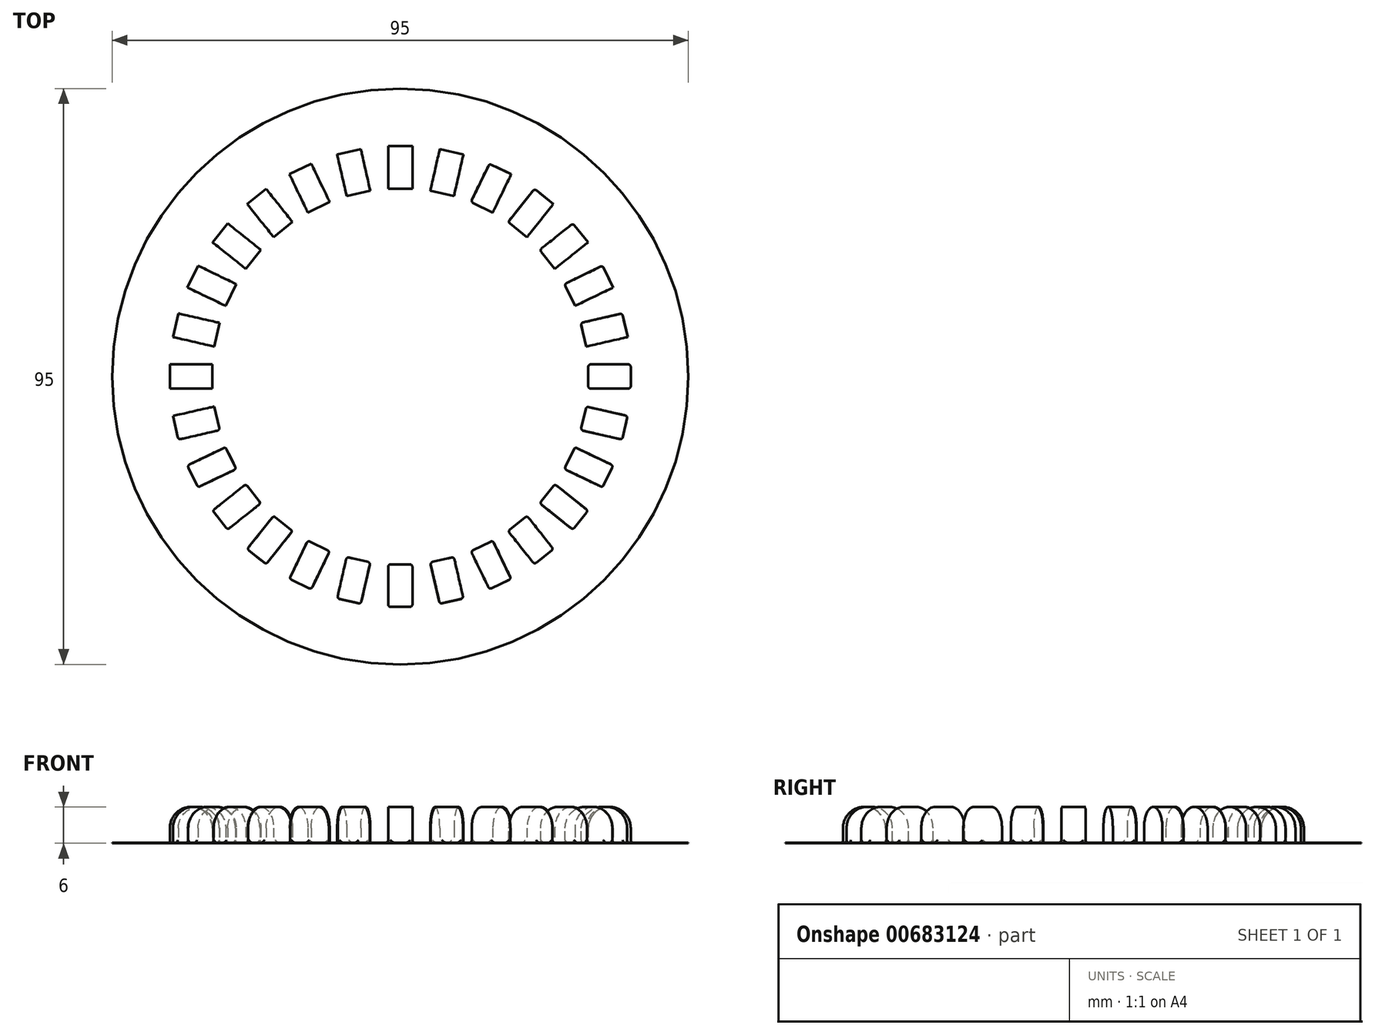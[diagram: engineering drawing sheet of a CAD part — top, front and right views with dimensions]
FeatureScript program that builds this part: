
annotation { "Feature Type Name" : "Feature", "Feature Type Description" : "" }
export const myFeature = defineFeature(function(context is Context, id is Id, definition is map)
    precondition{}
    {
        {
            var Q0;
            Q0=qCreatedBy(makeId("Top.planeOp"),FACE);
            var sketch = newSketch(context, id + "F0", { "sketchPlane" : qUnion([Q0])});
            skCircle(sketch, "E0", {"center": v(0, 0) * mm, "radius": 47.5 * mm});
            skSolve(sketch);
        }
        {
            var Q0;
            Q0=makeQuery(id+"F0.imprint","IMPRINT",FACE,{"disambiguationData":[TD([[makeQuery(id+"F0.imprint","IMPRINT",EDGE,{"derivedFrom":sQuery(id+"F0.wireOp",EDGE,"E0")}),1.0]])]});
            extrude(context, id + "F1", {"entities" : qUnion([Q0]), "depth" : .1 * mm, "offsetDistance" : 25 * mm});
        }
        {
            var Q0;
            Q0=qCreatedBy(makeId("Top.planeOp"),FACE);
            var sketch = newSketch(context, id + "F2", { "sketchPlane" : qUnion([Q0])});
            skLineSegment(sketch, "E1", {"start": v(0, 0) * mm, "end": v(0, 49.65) * mm, "construction": true});
            skLineSegment(sketch, "E2.bottom", {"start": v(-2, 38) * mm, "end": v(2, 38) * mm});
            skLineSegment(sketch, "E2.top", {"start": v(-2, 31) * mm, "end": v(2, 31) * mm});
            skLineSegment(sketch, "E2.left", {"start": v(-2, 38) * mm, "end": v(-2, 31) * mm});
            skLineSegment(sketch, "E2.right", {"start": v(2, 38) * mm, "end": v(2, 31) * mm});
            skPoint(sketch, "E3", {"position": v(0, 38) * mm});
            skPoint(sketch, "E4.1.0", {"position": v(-8.46, 37.05) * mm});
            skLineSegment(sketch, "E4.1.1", {"start": v(-8.85, 29.78) * mm, "end": v(-4.95, 30.67) * mm});
            skLineSegment(sketch, "E4.1.2", {"start": v(-10.4, 36.6) * mm, "end": v(-8.85, 29.78) * mm});
            skLineSegment(sketch, "E4.1.3", {"start": v(-6.5, 37.5) * mm, "end": v(-4.95, 30.67) * mm});
            skLineSegment(sketch, "E4.1.4", {"start": v(-10.4, 36.6) * mm, "end": v(-6.5, 37.5) * mm});
            skPoint(sketch, "E4.2.0", {"position": v(-16.49, 34.24) * mm});
            skLineSegment(sketch, "E4.2.1", {"start": v(-15.25, 27.06) * mm, "end": v(-11.65, 28.8) * mm});
            skLineSegment(sketch, "E4.2.2", {"start": v(-18.29, 33.37) * mm, "end": v(-15.25, 27.06) * mm});
            skLineSegment(sketch, "E4.2.3", {"start": v(-14.69, 35.1) * mm, "end": v(-11.65, 28.8) * mm});
            skLineSegment(sketch, "E4.2.4", {"start": v(-18.29, 33.37) * mm, "end": v(-14.69, 35.1) * mm});
            skPoint(sketch, "E4.center", {"position": v(0, 0) * mm});
            skLineSegment(sketch, "E5.1.3.0", {"start": v(-20.9, 22.99) * mm, "end": v(-17.76, 25.48) * mm});
            skPoint(sketch, "E5.2.3.0", {"position": v(-23.7, 29.7) * mm});
            skLineSegment(sketch, "E5.4.3.0", {"start": v(-25.26, 28.46) * mm, "end": v(-20.9, 22.99) * mm});
            skLineSegment(sketch, "E5.7.3.0", {"start": v(-22.13, 30.96) * mm, "end": v(-17.76, 25.48) * mm});
            skLineSegment(sketch, "E5.10.3.0", {"start": v(-25.26, 28.46) * mm, "end": v(-22.13, 30.96) * mm});
            skLineSegment(sketch, "E5.1.4.0", {"start": v(-25.48, 17.76) * mm, "end": v(-22.99, 20.9) * mm});
            skPoint(sketch, "E5.2.4.0", {"position": v(-29.7, 23.7) * mm});
            skLineSegment(sketch, "E5.4.4.0", {"start": v(-30.96, 22.13) * mm, "end": v(-25.48, 17.76) * mm});
            skLineSegment(sketch, "E5.7.4.0", {"start": v(-28.46, 25.26) * mm, "end": v(-22.99, 20.9) * mm});
            skLineSegment(sketch, "E5.10.4.0", {"start": v(-30.96, 22.13) * mm, "end": v(-28.46, 25.26) * mm});
            skLineSegment(sketch, "E5.1.5.0", {"start": v(-28.8, 11.65) * mm, "end": v(-27.06, 15.25) * mm});
            skPoint(sketch, "E5.2.5.0", {"position": v(-34.24, 16.49) * mm});
            skLineSegment(sketch, "E5.4.5.0", {"start": v(-35.1, 14.69) * mm, "end": v(-28.8, 11.65) * mm});
            skLineSegment(sketch, "E5.7.5.0", {"start": v(-33.37, 18.29) * mm, "end": v(-27.06, 15.25) * mm});
            skLineSegment(sketch, "E5.10.5.0", {"start": v(-35.1, 14.69) * mm, "end": v(-33.37, 18.29) * mm});
            skLineSegment(sketch, "E5.1.6.0", {"start": v(-30.67, 4.95) * mm, "end": v(-29.78, 8.85) * mm});
            skPoint(sketch, "E5.2.6.0", {"position": v(-37.05, 8.46) * mm});
            skLineSegment(sketch, "E5.4.6.0", {"start": v(-37.5, 6.5) * mm, "end": v(-30.67, 4.95) * mm});
            skLineSegment(sketch, "E5.7.6.0", {"start": v(-36.6, 10.4) * mm, "end": v(-29.78, 8.85) * mm});
            skLineSegment(sketch, "E5.10.6.0", {"start": v(-37.5, 6.5) * mm, "end": v(-36.6, 10.4) * mm});
            skLineSegment(sketch, "E5.1.7.0", {"start": v(-31, -2) * mm, "end": v(-31, 2) * mm});
            skPoint(sketch, "E5.2.7.0", {"position": v(-38, 0) * mm});
            skLineSegment(sketch, "E5.4.7.0", {"start": v(-38, -2) * mm, "end": v(-31, -2) * mm});
            skLineSegment(sketch, "E5.7.7.0", {"start": v(-38, 2) * mm, "end": v(-31, 2) * mm});
            skLineSegment(sketch, "E5.10.7.0", {"start": v(-38, -2) * mm, "end": v(-38, 2) * mm});
            skLineSegment(sketch, "E5.1.8.0", {"start": v(-29.78, -8.85) * mm, "end": v(-30.67, -4.95) * mm});
            skPoint(sketch, "E5.2.8.0", {"position": v(-37.05, -8.46) * mm});
            skLineSegment(sketch, "E5.4.8.0", {"start": v(-36.6, -10.4) * mm, "end": v(-29.78, -8.85) * mm});
            skLineSegment(sketch, "E5.7.8.0", {"start": v(-37.5, -6.5) * mm, "end": v(-30.67, -4.95) * mm});
            skLineSegment(sketch, "E5.10.8.0", {"start": v(-36.6, -10.4) * mm, "end": v(-37.5, -6.5) * mm});
            skLineSegment(sketch, "E5.1.9.0", {"start": v(-27.06, -15.25) * mm, "end": v(-28.8, -11.65) * mm});
            skPoint(sketch, "E5.2.9.0", {"position": v(-34.24, -16.49) * mm});
            skLineSegment(sketch, "E5.4.9.0", {"start": v(-33.37, -18.29) * mm, "end": v(-27.06, -15.25) * mm});
            skLineSegment(sketch, "E5.7.9.0", {"start": v(-35.1, -14.69) * mm, "end": v(-28.8, -11.65) * mm});
            skLineSegment(sketch, "E5.10.9.0", {"start": v(-33.37, -18.29) * mm, "end": v(-35.1, -14.69) * mm});
            skLineSegment(sketch, "E5.1.10.0", {"start": v(-22.99, -20.9) * mm, "end": v(-25.48, -17.76) * mm});
            skPoint(sketch, "E5.2.10.0", {"position": v(-29.7, -23.7) * mm});
            skLineSegment(sketch, "E5.4.10.0", {"start": v(-28.46, -25.26) * mm, "end": v(-22.99, -20.9) * mm});
            skLineSegment(sketch, "E5.7.10.0", {"start": v(-30.96, -22.13) * mm, "end": v(-25.48, -17.76) * mm});
            skLineSegment(sketch, "E5.10.10.0", {"start": v(-28.46, -25.26) * mm, "end": v(-30.96, -22.13) * mm});
            skLineSegment(sketch, "E5.1.11.0", {"start": v(-17.76, -25.48) * mm, "end": v(-20.9, -22.99) * mm});
            skPoint(sketch, "E5.2.11.0", {"position": v(-23.7, -29.7) * mm});
            skLineSegment(sketch, "E5.4.11.0", {"start": v(-22.13, -30.96) * mm, "end": v(-17.76, -25.48) * mm});
            skLineSegment(sketch, "E5.7.11.0", {"start": v(-25.26, -28.46) * mm, "end": v(-20.9, -22.99) * mm});
            skLineSegment(sketch, "E5.10.11.0", {"start": v(-22.13, -30.96) * mm, "end": v(-25.26, -28.46) * mm});
            skLineSegment(sketch, "E5.1.12.0", {"start": v(-11.65, -28.8) * mm, "end": v(-15.25, -27.06) * mm});
            skPoint(sketch, "E5.2.12.0", {"position": v(-16.49, -34.24) * mm});
            skLineSegment(sketch, "E5.4.12.0", {"start": v(-14.69, -35.1) * mm, "end": v(-11.65, -28.8) * mm});
            skLineSegment(sketch, "E5.7.12.0", {"start": v(-18.29, -33.37) * mm, "end": v(-15.25, -27.06) * mm});
            skLineSegment(sketch, "E5.10.12.0", {"start": v(-14.69, -35.1) * mm, "end": v(-18.29, -33.37) * mm});
            skLineSegment(sketch, "E5.1.13.0", {"start": v(-4.95, -30.67) * mm, "end": v(-8.85, -29.78) * mm});
            skPoint(sketch, "E5.2.13.0", {"position": v(-8.46, -37.05) * mm});
            skLineSegment(sketch, "E5.4.13.0", {"start": v(-6.5, -37.5) * mm, "end": v(-4.95, -30.67) * mm});
            skLineSegment(sketch, "E5.7.13.0", {"start": v(-10.4, -36.6) * mm, "end": v(-8.85, -29.78) * mm});
            skLineSegment(sketch, "E5.10.13.0", {"start": v(-6.5, -37.5) * mm, "end": v(-10.4, -36.6) * mm});
            skLineSegment(sketch, "E5.1.14.0", {"start": v(2, -31) * mm, "end": v(-2, -31) * mm});
            skPoint(sketch, "E5.2.14.0", {"position": v(0, -38) * mm});
            skLineSegment(sketch, "E5.4.14.0", {"start": v(2, -38) * mm, "end": v(2, -31) * mm});
            skLineSegment(sketch, "E5.7.14.0", {"start": v(-2, -38) * mm, "end": v(-2, -31) * mm});
            skLineSegment(sketch, "E5.10.14.0", {"start": v(2, -38) * mm, "end": v(-2, -38) * mm});
            skLineSegment(sketch, "E5.1.15.0", {"start": v(8.85, -29.78) * mm, "end": v(4.95, -30.67) * mm});
            skPoint(sketch, "E5.2.15.0", {"position": v(8.46, -37.05) * mm});
            skLineSegment(sketch, "E5.4.15.0", {"start": v(10.4, -36.6) * mm, "end": v(8.85, -29.78) * mm});
            skLineSegment(sketch, "E5.7.15.0", {"start": v(6.5, -37.5) * mm, "end": v(4.95, -30.67) * mm});
            skLineSegment(sketch, "E5.10.15.0", {"start": v(10.4, -36.6) * mm, "end": v(6.5, -37.5) * mm});
            skLineSegment(sketch, "E5.1.16.0", {"start": v(15.25, -27.06) * mm, "end": v(11.65, -28.8) * mm});
            skPoint(sketch, "E5.2.16.0", {"position": v(16.49, -34.24) * mm});
            skLineSegment(sketch, "E5.4.16.0", {"start": v(18.29, -33.37) * mm, "end": v(15.25, -27.06) * mm});
            skLineSegment(sketch, "E5.7.16.0", {"start": v(14.69, -35.1) * mm, "end": v(11.65, -28.8) * mm});
            skLineSegment(sketch, "E5.10.16.0", {"start": v(18.29, -33.37) * mm, "end": v(14.69, -35.1) * mm});
            skLineSegment(sketch, "E5.1.17.0", {"start": v(20.9, -22.99) * mm, "end": v(17.76, -25.48) * mm});
            skPoint(sketch, "E5.2.17.0", {"position": v(23.7, -29.7) * mm});
            skLineSegment(sketch, "E5.4.17.0", {"start": v(25.26, -28.46) * mm, "end": v(20.9, -22.99) * mm});
            skLineSegment(sketch, "E5.7.17.0", {"start": v(22.13, -30.96) * mm, "end": v(17.76, -25.48) * mm});
            skLineSegment(sketch, "E5.10.17.0", {"start": v(25.26, -28.46) * mm, "end": v(22.13, -30.96) * mm});
            skLineSegment(sketch, "E5.1.18.0", {"start": v(25.48, -17.76) * mm, "end": v(22.99, -20.9) * mm});
            skPoint(sketch, "E5.2.18.0", {"position": v(29.7, -23.7) * mm});
            skLineSegment(sketch, "E5.4.18.0", {"start": v(30.96, -22.13) * mm, "end": v(25.48, -17.76) * mm});
            skLineSegment(sketch, "E5.7.18.0", {"start": v(28.46, -25.26) * mm, "end": v(22.99, -20.9) * mm});
            skLineSegment(sketch, "E5.10.18.0", {"start": v(30.96, -22.13) * mm, "end": v(28.46, -25.26) * mm});
            skLineSegment(sketch, "E5.1.19.0", {"start": v(28.8, -11.65) * mm, "end": v(27.06, -15.25) * mm});
            skPoint(sketch, "E5.2.19.0", {"position": v(34.24, -16.49) * mm});
            skLineSegment(sketch, "E5.4.19.0", {"start": v(35.1, -14.69) * mm, "end": v(28.8, -11.65) * mm});
            skLineSegment(sketch, "E5.7.19.0", {"start": v(33.37, -18.29) * mm, "end": v(27.06, -15.25) * mm});
            skLineSegment(sketch, "E5.10.19.0", {"start": v(35.1, -14.69) * mm, "end": v(33.37, -18.29) * mm});
            skLineSegment(sketch, "E5.1.20.0", {"start": v(30.67, -4.95) * mm, "end": v(29.78, -8.85) * mm});
            skPoint(sketch, "E5.2.20.0", {"position": v(37.05, -8.46) * mm});
            skLineSegment(sketch, "E5.4.20.0", {"start": v(37.5, -6.5) * mm, "end": v(30.67, -4.95) * mm});
            skLineSegment(sketch, "E5.7.20.0", {"start": v(36.6, -10.4) * mm, "end": v(29.78, -8.85) * mm});
            skLineSegment(sketch, "E5.10.20.0", {"start": v(37.5, -6.5) * mm, "end": v(36.6, -10.4) * mm});
            skLineSegment(sketch, "E5.1.21.0", {"start": v(31, 2) * mm, "end": v(31, -2) * mm});
            skPoint(sketch, "E5.2.21.0", {"position": v(38, 0) * mm});
            skLineSegment(sketch, "E5.4.21.0", {"start": v(38, 2) * mm, "end": v(31, 2) * mm});
            skLineSegment(sketch, "E5.7.21.0", {"start": v(38, -2) * mm, "end": v(31, -2) * mm});
            skLineSegment(sketch, "E5.10.21.0", {"start": v(38, 2) * mm, "end": v(38, -2) * mm});
            skLineSegment(sketch, "E5.1.22.0", {"start": v(29.78, 8.85) * mm, "end": v(30.67, 4.95) * mm});
            skPoint(sketch, "E5.2.22.0", {"position": v(37.05, 8.46) * mm});
            skLineSegment(sketch, "E5.4.22.0", {"start": v(36.6, 10.4) * mm, "end": v(29.78, 8.85) * mm});
            skLineSegment(sketch, "E5.7.22.0", {"start": v(37.5, 6.5) * mm, "end": v(30.67, 4.95) * mm});
            skLineSegment(sketch, "E5.10.22.0", {"start": v(36.6, 10.4) * mm, "end": v(37.5, 6.5) * mm});
            skLineSegment(sketch, "E5.1.23.0", {"start": v(27.06, 15.25) * mm, "end": v(28.8, 11.65) * mm});
            skPoint(sketch, "E5.2.23.0", {"position": v(34.24, 16.49) * mm});
            skLineSegment(sketch, "E5.4.23.0", {"start": v(33.37, 18.29) * mm, "end": v(27.06, 15.25) * mm});
            skLineSegment(sketch, "E5.7.23.0", {"start": v(35.1, 14.69) * mm, "end": v(28.8, 11.65) * mm});
            skLineSegment(sketch, "E5.10.23.0", {"start": v(33.37, 18.29) * mm, "end": v(35.1, 14.69) * mm});
            skLineSegment(sketch, "E5.1.24.0", {"start": v(22.99, 20.9) * mm, "end": v(25.48, 17.76) * mm});
            skPoint(sketch, "E5.2.24.0", {"position": v(29.7, 23.7) * mm});
            skLineSegment(sketch, "E5.4.24.0", {"start": v(28.46, 25.26) * mm, "end": v(22.99, 20.9) * mm});
            skLineSegment(sketch, "E5.7.24.0", {"start": v(30.96, 22.13) * mm, "end": v(25.48, 17.76) * mm});
            skLineSegment(sketch, "E5.10.24.0", {"start": v(28.46, 25.26) * mm, "end": v(30.96, 22.13) * mm});
            skLineSegment(sketch, "E5.1.25.0", {"start": v(17.76, 25.48) * mm, "end": v(20.9, 22.99) * mm});
            skPoint(sketch, "E5.2.25.0", {"position": v(23.7, 29.7) * mm});
            skLineSegment(sketch, "E5.4.25.0", {"start": v(22.13, 30.96) * mm, "end": v(17.76, 25.48) * mm});
            skLineSegment(sketch, "E5.7.25.0", {"start": v(25.26, 28.46) * mm, "end": v(20.9, 22.99) * mm});
            skLineSegment(sketch, "E5.10.25.0", {"start": v(22.13, 30.96) * mm, "end": v(25.26, 28.46) * mm});
            skLineSegment(sketch, "E5.1.26.0", {"start": v(11.65, 28.8) * mm, "end": v(15.25, 27.06) * mm});
            skPoint(sketch, "E5.2.26.0", {"position": v(16.49, 34.24) * mm});
            skLineSegment(sketch, "E5.4.26.0", {"start": v(14.69, 35.1) * mm, "end": v(11.65, 28.8) * mm});
            skLineSegment(sketch, "E5.7.26.0", {"start": v(18.29, 33.37) * mm, "end": v(15.25, 27.06) * mm});
            skLineSegment(sketch, "E5.10.26.0", {"start": v(14.69, 35.1) * mm, "end": v(18.29, 33.37) * mm});
            skLineSegment(sketch, "E5.1.27.0", {"start": v(4.95, 30.67) * mm, "end": v(8.85, 29.78) * mm});
            skPoint(sketch, "E5.2.27.0", {"position": v(8.46, 37.05) * mm});
            skLineSegment(sketch, "E5.4.27.0", {"start": v(6.5, 37.5) * mm, "end": v(4.95, 30.67) * mm});
            skLineSegment(sketch, "E5.7.27.0", {"start": v(10.4, 36.6) * mm, "end": v(8.85, 29.78) * mm});
            skLineSegment(sketch, "E5.10.27.0", {"start": v(6.5, 37.5) * mm, "end": v(10.4, 36.6) * mm});
            skSolve(sketch);
        }
        {
            var Q0;
            Q0=qSketchRegion(id+"F2",true);
            extrude(context, id + "F3", {"entities" : qUnion([Q0]), "operationType" : NewBodyOperationType.ADD, "depth" : 6 * mm, "offsetDistance" : 25 * mm});
        }
        {
            var Q0;
            Q0=makeQuery(id+"F3.opExtrude","CAP_EDGE",EDGE,{"disambiguationData":[OSD([sQuery(id+"F2.wireOp",EDGE,"E4.1.1")])],"isStart":false});
            var Q1;
            Q1=makeQuery(id+"F3.opExtrude","CAP_EDGE",EDGE,{"disambiguationData":[OSD([sQuery(id+"F2.wireOp",EDGE,"E2.top")])],"isStart":false});
            var Q2;
            Q2=makeQuery(id+"F3.opExtrude","CAP_EDGE",EDGE,{"disambiguationData":[OSD([sQuery(id+"F2.wireOp",EDGE,"E5.1.27.0")])],"isStart":false});
            var Q3;
            Q3=makeQuery(id+"F3.opExtrude","CAP_EDGE",EDGE,{"disambiguationData":[OSD([sQuery(id+"F2.wireOp",EDGE,"E5.1.26.0")])],"isStart":false});
            var Q4;
            Q4=makeQuery(id+"F3.opExtrude","CAP_EDGE",EDGE,{"disambiguationData":[OSD([sQuery(id+"F2.wireOp",EDGE,"E5.1.25.0")])],"isStart":false});
            var Q5;
            Q5=makeQuery(id+"F3.opExtrude","CAP_EDGE",EDGE,{"disambiguationData":[OSD([sQuery(id+"F2.wireOp",EDGE,"E5.1.24.0")])],"isStart":false});
            var Q6;
            Q6=makeQuery(id+"F3.opExtrude","CAP_EDGE",EDGE,{"disambiguationData":[OSD([sQuery(id+"F2.wireOp",EDGE,"E5.1.23.0")])],"isStart":false});
            var Q7;
            Q7=makeQuery(id+"F3.opExtrude","CAP_EDGE",EDGE,{"disambiguationData":[OSD([sQuery(id+"F2.wireOp",EDGE,"E5.1.22.0")])],"isStart":false});
            var Q8;
            Q8=makeQuery(id+"F3.opExtrude","CAP_EDGE",EDGE,{"disambiguationData":[OSD([sQuery(id+"F2.wireOp",EDGE,"E5.1.21.0")])],"isStart":false});
            var Q9;
            Q9=makeQuery(id+"F3.opExtrude","CAP_EDGE",EDGE,{"disambiguationData":[OSD([sQuery(id+"F2.wireOp",EDGE,"E5.1.20.0")])],"isStart":false});
            var Q10;
            Q10=makeQuery(id+"F3.opExtrude","CAP_EDGE",EDGE,{"disambiguationData":[OSD([sQuery(id+"F2.wireOp",EDGE,"E5.1.19.0")])],"isStart":false});
            var Q11;
            Q11=makeQuery(id+"F3.opExtrude","CAP_EDGE",EDGE,{"disambiguationData":[OSD([sQuery(id+"F2.wireOp",EDGE,"E5.1.18.0")])],"isStart":false});
            var Q12;
            Q12=makeQuery(id+"F3.opExtrude","CAP_EDGE",EDGE,{"disambiguationData":[OSD([sQuery(id+"F2.wireOp",EDGE,"E5.1.17.0")])],"isStart":false});
            var Q13;
            Q13=makeQuery(id+"F3.opExtrude","CAP_EDGE",EDGE,{"disambiguationData":[OSD([sQuery(id+"F2.wireOp",EDGE,"E5.1.16.0")])],"isStart":false});
            var Q14;
            Q14=makeQuery(id+"F3.opExtrude","CAP_EDGE",EDGE,{"disambiguationData":[OSD([sQuery(id+"F2.wireOp",EDGE,"E5.1.15.0")])],"isStart":false});
            var Q15;
            Q15=makeQuery(id+"F3.opExtrude","CAP_EDGE",EDGE,{"disambiguationData":[OSD([sQuery(id+"F2.wireOp",EDGE,"E5.1.14.0")])],"isStart":false});
            var Q16;
            Q16=makeQuery(id+"F3.opExtrude","CAP_EDGE",EDGE,{"disambiguationData":[OSD([sQuery(id+"F2.wireOp",EDGE,"E5.1.13.0")])],"isStart":false});
            var Q17;
            Q17=makeQuery(id+"F3.opExtrude","CAP_EDGE",EDGE,{"disambiguationData":[OSD([sQuery(id+"F2.wireOp",EDGE,"E5.1.12.0")])],"isStart":false});
            var Q18;
            Q18=makeQuery(id+"F3.opExtrude","CAP_EDGE",EDGE,{"disambiguationData":[OSD([sQuery(id+"F2.wireOp",EDGE,"E5.1.11.0")])],"isStart":false});
            var Q19;
            Q19=makeQuery(id+"F3.opExtrude","CAP_EDGE",EDGE,{"disambiguationData":[OSD([sQuery(id+"F2.wireOp",EDGE,"E5.1.10.0")])],"isStart":false});
            var Q20;
            Q20=makeQuery(id+"F3.opExtrude","CAP_EDGE",EDGE,{"disambiguationData":[OSD([sQuery(id+"F2.wireOp",EDGE,"E5.1.9.0")])],"isStart":false});
            var Q21;
            Q21=makeQuery(id+"F3.opExtrude","CAP_EDGE",EDGE,{"disambiguationData":[OSD([sQuery(id+"F2.wireOp",EDGE,"E5.1.8.0")])],"isStart":false});
            var Q22;
            Q22=makeQuery(id+"F3.opExtrude","CAP_EDGE",EDGE,{"disambiguationData":[OSD([sQuery(id+"F2.wireOp",EDGE,"E5.1.7.0")])],"isStart":false});
            var Q23;
            Q23=makeQuery(id+"F3.opExtrude","CAP_EDGE",EDGE,{"disambiguationData":[OSD([sQuery(id+"F2.wireOp",EDGE,"E5.1.6.0")])],"isStart":false});
            var Q24;
            Q24=makeQuery(id+"F3.opExtrude","CAP_EDGE",EDGE,{"disambiguationData":[OSD([sQuery(id+"F2.wireOp",EDGE,"E5.1.5.0")])],"isStart":false});
            var Q25;
            Q25=makeQuery(id+"F3.opExtrude","CAP_EDGE",EDGE,{"disambiguationData":[OSD([sQuery(id+"F2.wireOp",EDGE,"E5.1.4.0")])],"isStart":false});
            var Q26;
            Q26=makeQuery(id+"F3.opExtrude","CAP_EDGE",EDGE,{"disambiguationData":[OSD([sQuery(id+"F2.wireOp",EDGE,"E5.1.3.0")])],"isStart":false});
            var Q27;
            Q27=makeQuery(id+"F3.opExtrude","CAP_EDGE",EDGE,{"disambiguationData":[OSD([sQuery(id+"F2.wireOp",EDGE,"E4.2.1")])],"isStart":false});
            var Q28;
            Q28=makeQuery(id+"F3.opExtrude","CAP_EDGE",EDGE,{"disambiguationData":[OSD([sQuery(id+"F2.wireOp",EDGE,"E4.1.4")])],"isStart":false});
            var Q29;
            Q29=makeQuery(id+"F3.opExtrude","CAP_EDGE",EDGE,{"disambiguationData":[OSD([sQuery(id+"F2.wireOp",EDGE,"E2.bottom")])],"isStart":false});
            var Q30;
            Q30=makeQuery(id+"F3.opExtrude","CAP_EDGE",EDGE,{"disambiguationData":[OSD([sQuery(id+"F2.wireOp",EDGE,"E5.10.27.0")])],"isStart":false});
            var Q31;
            Q31=makeQuery(id+"F3.opExtrude","CAP_EDGE",EDGE,{"disambiguationData":[OSD([sQuery(id+"F2.wireOp",EDGE,"E5.10.26.0")])],"isStart":false});
            var Q32;
            Q32=makeQuery(id+"F3.opExtrude","CAP_EDGE",EDGE,{"disambiguationData":[OSD([sQuery(id+"F2.wireOp",EDGE,"E5.10.25.0")])],"isStart":false});
            var Q33;
            Q33=makeQuery(id+"F3.opExtrude","CAP_EDGE",EDGE,{"disambiguationData":[OSD([sQuery(id+"F2.wireOp",EDGE,"E5.10.24.0")])],"isStart":false});
            var Q34;
            Q34=makeQuery(id+"F3.opExtrude","CAP_EDGE",EDGE,{"disambiguationData":[OSD([sQuery(id+"F2.wireOp",EDGE,"E5.10.23.0")])],"isStart":false});
            var Q35;
            Q35=makeQuery(id+"F3.opExtrude","CAP_EDGE",EDGE,{"disambiguationData":[OSD([sQuery(id+"F2.wireOp",EDGE,"E5.10.22.0")])],"isStart":false});
            var Q36;
            Q36=makeQuery(id+"F3.opExtrude","CAP_EDGE",EDGE,{"disambiguationData":[OSD([sQuery(id+"F2.wireOp",EDGE,"E5.10.21.0")])],"isStart":false});
            var Q37;
            Q37=makeQuery(id+"F3.opExtrude","CAP_EDGE",EDGE,{"disambiguationData":[OSD([sQuery(id+"F2.wireOp",EDGE,"E5.10.20.0")])],"isStart":false});
            var Q38;
            Q38=makeQuery(id+"F3.opExtrude","CAP_EDGE",EDGE,{"disambiguationData":[OSD([sQuery(id+"F2.wireOp",EDGE,"E5.10.19.0")])],"isStart":false});
            var Q39;
            Q39=makeQuery(id+"F3.opExtrude","CAP_EDGE",EDGE,{"disambiguationData":[OSD([sQuery(id+"F2.wireOp",EDGE,"E5.10.18.0")])],"isStart":false});
            var Q40;
            Q40=makeQuery(id+"F3.opExtrude","CAP_EDGE",EDGE,{"disambiguationData":[OSD([sQuery(id+"F2.wireOp",EDGE,"E5.10.17.0")])],"isStart":false});
            var Q41;
            Q41=makeQuery(id+"F3.opExtrude","CAP_EDGE",EDGE,{"disambiguationData":[OSD([sQuery(id+"F2.wireOp",EDGE,"E5.10.16.0")])],"isStart":false});
            var Q42;
            Q42=makeQuery(id+"F3.opExtrude","CAP_EDGE",EDGE,{"disambiguationData":[OSD([sQuery(id+"F2.wireOp",EDGE,"E5.10.15.0")])],"isStart":false});
            var Q43;
            Q43=makeQuery(id+"F3.opExtrude","CAP_EDGE",EDGE,{"disambiguationData":[OSD([sQuery(id+"F2.wireOp",EDGE,"E5.10.14.0")])],"isStart":false});
            var Q44;
            Q44=makeQuery(id+"F3.opExtrude","CAP_EDGE",EDGE,{"disambiguationData":[OSD([sQuery(id+"F2.wireOp",EDGE,"E5.10.13.0")])],"isStart":false});
            var Q45;
            Q45=makeQuery(id+"F3.opExtrude","CAP_EDGE",EDGE,{"disambiguationData":[OSD([sQuery(id+"F2.wireOp",EDGE,"E5.10.12.0")])],"isStart":false});
            var Q46;
            Q46=makeQuery(id+"F3.opExtrude","CAP_EDGE",EDGE,{"disambiguationData":[OSD([sQuery(id+"F2.wireOp",EDGE,"E5.10.11.0")])],"isStart":false});
            var Q47;
            Q47=makeQuery(id+"F3.opExtrude","CAP_EDGE",EDGE,{"disambiguationData":[OSD([sQuery(id+"F2.wireOp",EDGE,"E5.10.10.0")])],"isStart":false});
            var Q48;
            Q48=makeQuery(id+"F3.opExtrude","CAP_EDGE",EDGE,{"disambiguationData":[OSD([sQuery(id+"F2.wireOp",EDGE,"E5.10.9.0")])],"isStart":false});
            var Q49;
            Q49=makeQuery(id+"F3.opExtrude","CAP_EDGE",EDGE,{"disambiguationData":[OSD([sQuery(id+"F2.wireOp",EDGE,"E5.10.8.0")])],"isStart":false});
            var Q50;
            Q50=makeQuery(id+"F3.opExtrude","CAP_EDGE",EDGE,{"disambiguationData":[OSD([sQuery(id+"F2.wireOp",EDGE,"E5.10.7.0")])],"isStart":false});
            var Q51;
            Q51=makeQuery(id+"F3.opExtrude","CAP_EDGE",EDGE,{"disambiguationData":[OSD([sQuery(id+"F2.wireOp",EDGE,"E5.10.6.0")])],"isStart":false});
            var Q52;
            Q52=makeQuery(id+"F3.opExtrude","CAP_EDGE",EDGE,{"disambiguationData":[OSD([sQuery(id+"F2.wireOp",EDGE,"E5.10.5.0")])],"isStart":false});
            var Q53;
            Q53=makeQuery(id+"F3.opExtrude","CAP_EDGE",EDGE,{"disambiguationData":[OSD([sQuery(id+"F2.wireOp",EDGE,"E5.10.4.0")])],"isStart":false});
            var Q54;
            Q54=makeQuery(id+"F3.opExtrude","CAP_EDGE",EDGE,{"disambiguationData":[OSD([sQuery(id+"F2.wireOp",EDGE,"E5.10.3.0")])],"isStart":false});
            var Q55;
            Q55=makeQuery(id+"F3.opExtrude","CAP_EDGE",EDGE,{"disambiguationData":[OSD([sQuery(id+"F2.wireOp",EDGE,"E4.2.4")])],"isStart":false});
            fillet(context, id + "F4", {"entities" : qUnion([Q0, Q1, Q2, Q3, Q4, Q5, Q6, Q7, Q8, Q9, Q10, Q11, Q12, Q13, Q14, Q15, Q16, Q17, Q18, Q19, Q20, Q21, Q22, Q23, Q24, Q25, Q26, Q27, Q28, Q29, Q30, Q31, Q32, Q33, Q34, Q35, Q36, Q37, Q38, Q39, Q40, Q41, Q42, Q43, Q44, Q45, Q46, Q47, Q48, Q49, Q50, Q51, Q52, Q53, Q54, Q55]), "radius" : 3.5 * mm, "tangentPropagation" : true, "allowEdgeOverflow" : false});
        }
        {
            var Q0;
            Q0=makeQuery(id+"F3.opExtrude","SWEPT_FACE",FACE,{"disambiguationData":[OSD([sQuery(id+"F2.wireOp",EDGE,"E5.4.26.0")])]});
            var Q1;
            Q1=makeQuery(id+"F3.opExtrude","SWEPT_FACE",FACE,{"disambiguationData":[OSD([sQuery(id+"F2.wireOp",EDGE,"E5.4.25.0")])]});
            var Q2;
            Q2=makeQuery(id+"F3.opExtrude","SWEPT_FACE",FACE,{"disambiguationData":[OSD([sQuery(id+"F2.wireOp",EDGE,"E5.4.24.0")])]});
            var Q3;
            Q3=makeQuery(id+"F3.opExtrude","SWEPT_FACE",FACE,{"disambiguationData":[OSD([sQuery(id+"F2.wireOp",EDGE,"E5.4.23.0")])]});
            var Q4;
            Q4=makeQuery(id+"F3.opExtrude","SWEPT_FACE",FACE,{"disambiguationData":[OSD([sQuery(id+"F2.wireOp",EDGE,"E5.4.22.0")])]});
            var Q5;
            Q5=makeQuery(id+"F3.opExtrude","SWEPT_FACE",FACE,{"disambiguationData":[OSD([sQuery(id+"F2.wireOp",EDGE,"E5.4.21.0")])]});
            var Q6;
            Q6=makeQuery(id+"F3.opExtrude","SWEPT_FACE",FACE,{"disambiguationData":[OSD([sQuery(id+"F2.wireOp",EDGE,"E5.4.20.0")])]});
            var Q7;
            Q7=makeQuery(id+"F3.opExtrude","SWEPT_FACE",FACE,{"disambiguationData":[OSD([sQuery(id+"F2.wireOp",EDGE,"E5.4.19.0")])]});
            var Q8;
            Q8=makeQuery(id+"F3.opExtrude","SWEPT_FACE",FACE,{"disambiguationData":[OSD([sQuery(id+"F2.wireOp",EDGE,"E5.4.18.0")])]});
            var Q9;
            Q9=makeQuery(id+"F3.opExtrude","SWEPT_FACE",FACE,{"disambiguationData":[OSD([sQuery(id+"F2.wireOp",EDGE,"E5.4.17.0")])]});
            var Q10;
            Q10=makeQuery(id+"F3.opExtrude","SWEPT_FACE",FACE,{"disambiguationData":[OSD([sQuery(id+"F2.wireOp",EDGE,"E5.4.16.0")])]});
            var Q11;
            Q11=makeQuery(id+"F3.opExtrude","SWEPT_FACE",FACE,{"disambiguationData":[OSD([sQuery(id+"F2.wireOp",EDGE,"E5.7.19.0")])]});
            var Q12;
            Q12=makeQuery(id+"F3.opExtrude","SWEPT_FACE",FACE,{"disambiguationData":[OSD([sQuery(id+"F2.wireOp",EDGE,"E5.7.20.0")])]});
            var Q13;
            Q13=makeQuery(id+"F3.opExtrude","SWEPT_FACE",FACE,{"disambiguationData":[OSD([sQuery(id+"F2.wireOp",EDGE,"E5.7.21.0")])]});
            var Q14;
            Q14=makeQuery(id+"F3.opExtrude","SWEPT_FACE",FACE,{"disambiguationData":[OSD([sQuery(id+"F2.wireOp",EDGE,"E5.7.18.0")])]});
            var Q15;
            Q15=makeQuery(id+"F3.opExtrude","SWEPT_FACE",FACE,{"disambiguationData":[OSD([sQuery(id+"F2.wireOp",EDGE,"E5.7.17.0")])]});
            var Q16;
            Q16=makeQuery(id+"F3.opExtrude","SWEPT_FACE",FACE,{"disambiguationData":[OSD([sQuery(id+"F2.wireOp",EDGE,"E5.7.16.0")])]});
            var Q17;
            Q17=makeQuery(id+"F3.opExtrude","SWEPT_FACE",FACE,{"disambiguationData":[OSD([sQuery(id+"F2.wireOp",EDGE,"E5.4.15.0")])]});
            var Q18;
            Q18=makeQuery(id+"F3.opExtrude","SWEPT_FACE",FACE,{"disambiguationData":[OSD([sQuery(id+"F2.wireOp",EDGE,"E5.7.15.0")])]});
            var Q19;
            Q19=makeQuery(id+"F3.opExtrude","SWEPT_FACE",FACE,{"disambiguationData":[OSD([sQuery(id+"F2.wireOp",EDGE,"E5.4.14.0")])]});
            var Q20;
            Q20=makeQuery(id+"F3.opExtrude","SWEPT_FACE",FACE,{"disambiguationData":[OSD([sQuery(id+"F2.wireOp",EDGE,"E5.7.14.0")])]});
            var Q21;
            Q21=makeQuery(id+"F3.opExtrude","SWEPT_FACE",FACE,{"disambiguationData":[OSD([sQuery(id+"F2.wireOp",EDGE,"E5.4.13.0")])]});
            var Q22;
            Q22=makeQuery(id+"F3.opExtrude","SWEPT_FACE",FACE,{"disambiguationData":[OSD([sQuery(id+"F2.wireOp",EDGE,"E5.7.13.0")])]});
            var Q23;
            Q23=makeQuery(id+"F3.opExtrude","SWEPT_FACE",FACE,{"disambiguationData":[OSD([sQuery(id+"F2.wireOp",EDGE,"E5.4.12.0")])]});
            var Q24;
            Q24=makeQuery(id+"F3.opExtrude","SWEPT_FACE",FACE,{"disambiguationData":[OSD([sQuery(id+"F2.wireOp",EDGE,"E5.7.12.0")])]});
            var Q25;
            Q25=makeQuery(id+"F3.opExtrude","SWEPT_FACE",FACE,{"disambiguationData":[OSD([sQuery(id+"F2.wireOp",EDGE,"E5.4.11.0")])]});
            var Q26;
            Q26=makeQuery(id+"F3.opExtrude","SWEPT_FACE",FACE,{"disambiguationData":[OSD([sQuery(id+"F2.wireOp",EDGE,"E5.7.11.0")])]});
            var Q27;
            Q27=makeQuery(id+"F3.opExtrude","SWEPT_FACE",FACE,{"disambiguationData":[OSD([sQuery(id+"F2.wireOp",EDGE,"E5.4.10.0")])]});
            var Q28;
            Q28=makeQuery(id+"F3.opExtrude","SWEPT_FACE",FACE,{"disambiguationData":[OSD([sQuery(id+"F2.wireOp",EDGE,"E5.7.10.0")])]});
            var Q29;
            Q29=makeQuery(id+"F3.opExtrude","SWEPT_FACE",FACE,{"disambiguationData":[OSD([sQuery(id+"F2.wireOp",EDGE,"E5.4.9.0")])]});
            var Q30;
            Q30=makeQuery(id+"F3.opExtrude","SWEPT_FACE",FACE,{"disambiguationData":[OSD([sQuery(id+"F2.wireOp",EDGE,"E5.7.9.0")])]});
            var Q31;
            Q31=makeQuery(id+"F3.opExtrude","SWEPT_FACE",FACE,{"disambiguationData":[OSD([sQuery(id+"F2.wireOp",EDGE,"E5.4.8.0")])]});
            fillet(context, id + "F5", {"entities" : qUnion([Q0, Q1, Q2, Q3, Q4, Q5, Q6, Q7, Q8, Q9, Q10, Q11, Q12, Q13, Q14, Q15, Q16, Q17, Q18, Q19, Q20, Q21, Q22, Q23, Q24, Q25, Q26, Q27, Q28, Q29, Q30, Q31]), "radius" : 0.4 * mm, "tangentPropagation" : true, "allowEdgeOverflow" : false});
        }
    });
